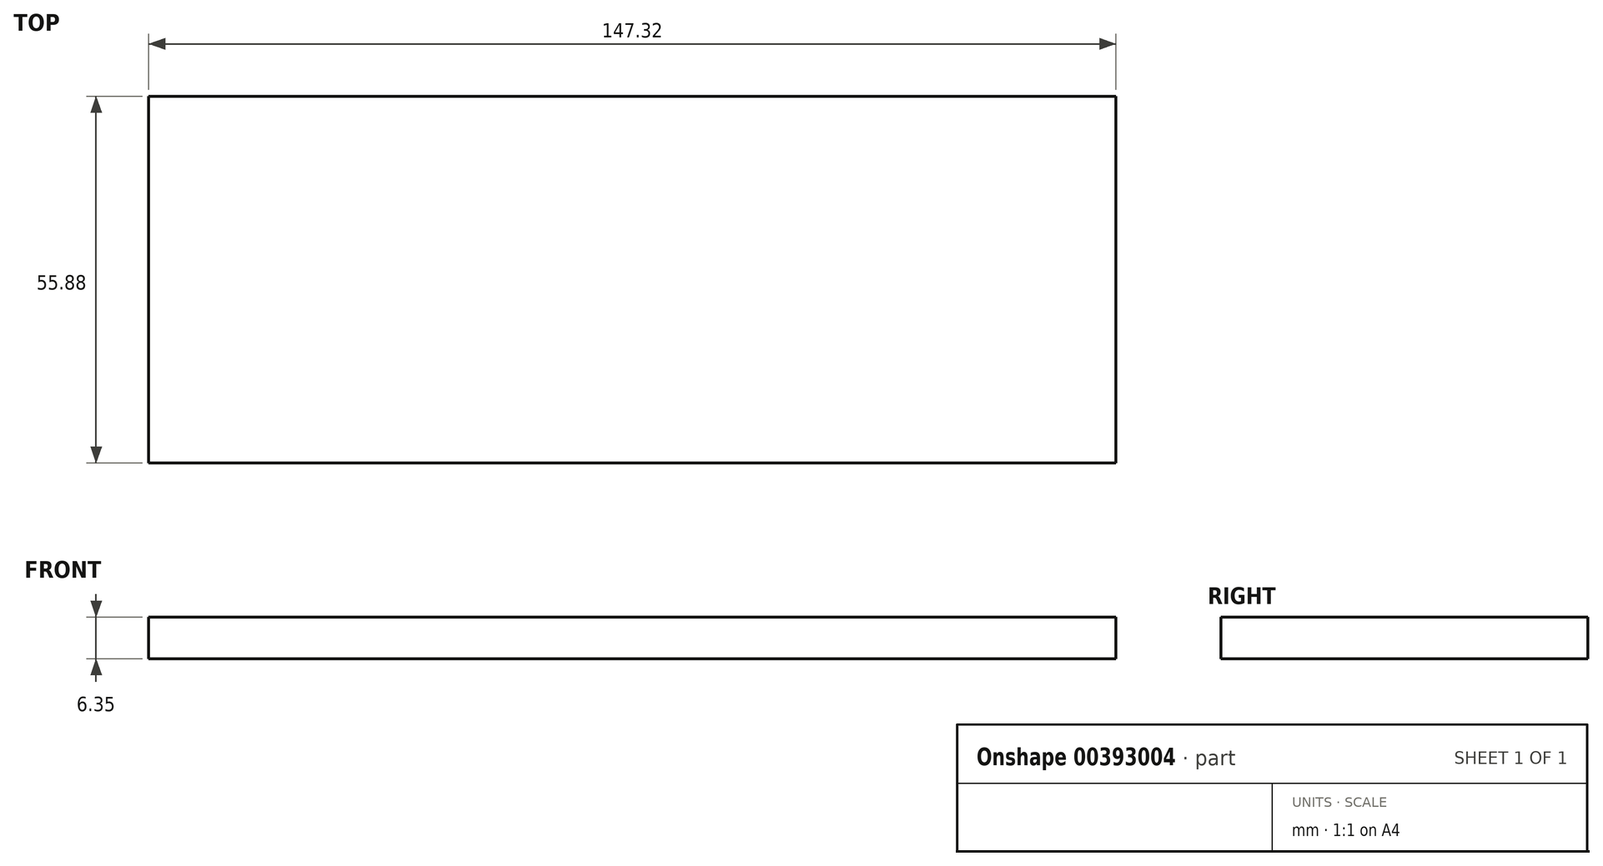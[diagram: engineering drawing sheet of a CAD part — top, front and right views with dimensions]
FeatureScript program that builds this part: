
annotation { "Feature Type Name" : "Feature", "Feature Type Description" : "" }
export const myFeature = defineFeature(function(context is Context, id is Id, definition is map)
    precondition{}
    {
        {
            var Q0;
            Q0=qCreatedBy(makeId("Top.planeOp"),FACE);
            var sketch = newSketch(context, id + "F0", { "sketchPlane" : qUnion([Q0])});
            skLineSegment(sketch, "E0.bottom", {"start": v(73.66, -27.94) * mm, "end": v(-73.66, -27.94) * mm});
            skLineSegment(sketch, "E0.top", {"start": v(73.66, 27.94) * mm, "end": v(-73.66, 27.94) * mm});
            skLineSegment(sketch, "E0.left", {"start": v(73.66, -27.94) * mm, "end": v(73.66, 27.94) * mm});
            skLineSegment(sketch, "E0.right", {"start": v(-73.66, -27.94) * mm, "end": v(-73.66, 27.94) * mm});
            skPoint(sketch, "E0.middle", {"position": v(0, 0) * mm});
            skSolve(sketch);
        }
        {
            var Q0;
            Q0 = qSketchRegion(id + "F0", true);
            extrude(context, id + "F1", {"entities" : qUnion([Q0]), "depth" : 6.35 * mm});
        }
    });
